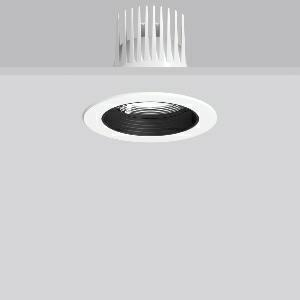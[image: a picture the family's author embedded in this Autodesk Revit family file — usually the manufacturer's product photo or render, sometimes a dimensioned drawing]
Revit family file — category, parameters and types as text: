
# Revit family: heledon_maxi_e_901789_002_2_4368
name_source: partatom
category: Lighting Fixtures
units: mm (PartAtom-declared; Revit-internal decimal feet)

## family parameters
Cut with Voids When Loaded = No
Host = Face
Light Source = No
Part Type = Normal
Room Calculation Point = No
Round Connector Dimension = Use Diameter
Shared = No

## types (1)
- HELEDON maxi E (1 x LED Modul 927 bakery, 2850 lm, 2700)
    Apparent Load = 33 VA
    Approval mark = CE
    CIE Flux Codes = 96 99 100 100 100
    Color Rendering = 90
    Color Temperature = 2700
    Default Elevation = 1800 mm
    Description = Series: HELEDON maxi
Round recessed downlight. Housing: die-cast aluminium, powder-coated. Black plastic ring and recessed LED to prevent glare from the side. Optical assembly with lens made of plastic (polycarbonate) for the best homogeneous light distribution - can be changed without tools. Special LED for illumination of pastries included. Suitable for Recessed ceiling mounting. Installation without tools thanks to spring fastening system. Including separate LED converter with connecting cable 600 mm.High quality converter without flickering and stroboscopic effect. Through-wiring box (5 pole) available as accessory. The following accessories can be mounted without use of tools: interchangeable lenses, decorative glasses, honeycomb louvre, clear and frosted diffusers, white interchangeable plastic ring. 
Colour: traffic white, matt (RAL 9016)
Diameter: 162 mm
Height: 3 mm
Cut-out diameter: 152 mm
Recess height: 200 mm
Luminaire: recess height: 135 mm
Lamp: LED
Socket: without socket
Colour temperature: bakery
Colour rendering index (CRI): 97
System power: 33 W
Rated luminous flux: 2850 lm
Luminous efficiency: 86 lm/W
Control gear: Regulated power supply
Protection class: II
Type of protection: IP 20
    Height = 0 mm  [stored 0 ft]
    Lamp = 1 x LED Modul 927 bakery
    Lamp Light Flux = 2850 lm
    Lamp count = 1
    Length = 162 mm
    Lifetime = 50000 h
    Luminous efficacy = 86 lm/W
    Manufacturer = RZB
    ModVariant = No
    Model = 901789.002.2
    Mounting Place = Ceiling
    Mounting Type = Recessed
    Number of Poles = 1
    OnlyDefault = Yes
    Power Factor = 1
    Product Name = HELEDON maxi E
    Product group = Recessed downlights
    ProductGroupID = 402
    Protection Class = Protection class II
    Protection Degree = IP 20
    RLX_Detail_Level = 1
    RLX_Emergency_Light_Flux = 0 lm
    RLX_Emergency_Type = 0
    RLX_Emergency_Type_DB = No
    RlxData = <blob elided: 121121 chars, md5=20e27017>
    Socket = socket
    Standby Power = 0 W
    System Light Flux = 2850 lm
    System Power = 33 W
    Type Comments = Product without accessories
    Type Image = 901663.002.jpg
    URL = http://relux.com
    VarID = ---
    Voltage = 230 V
    Voltage Range = 220-240 V
    Weight = 0.00 kg
    Width = 0 mm  [stored 0 ft]

note: [stored X ft] marks values corroborated as IEEE doubles in the binary element streams (Revit-internal decimal feet)

## geometry (parser evidence)
native form markers: Blend x4, Sweep x11
no freeform markers — native parametric forms only
